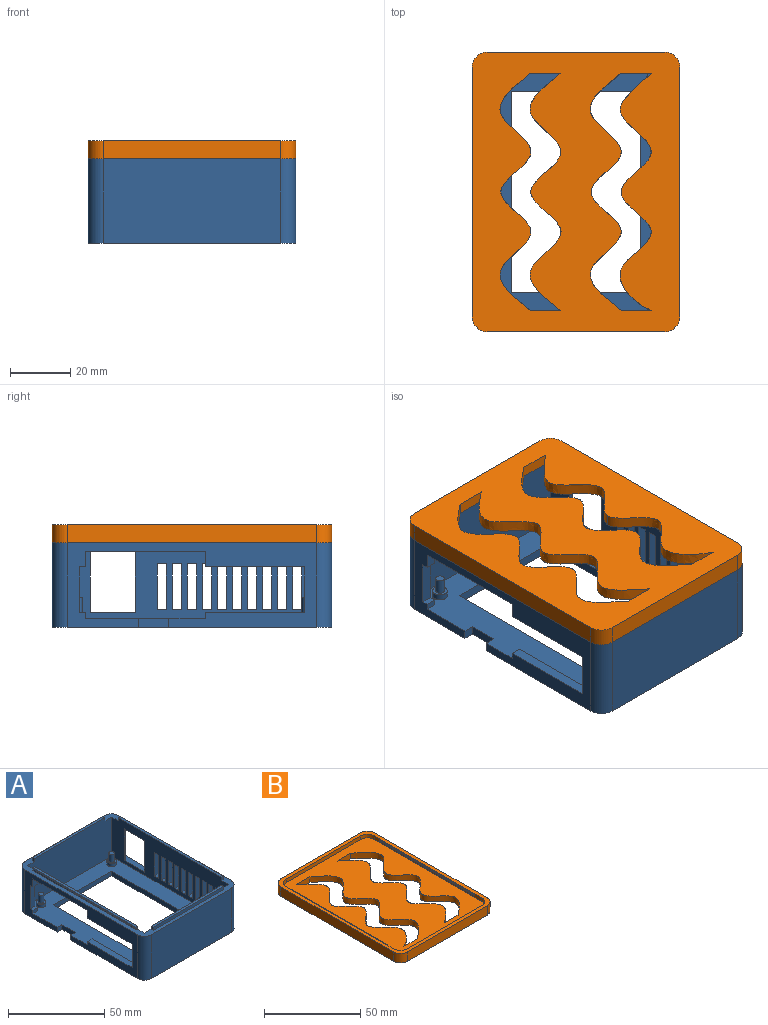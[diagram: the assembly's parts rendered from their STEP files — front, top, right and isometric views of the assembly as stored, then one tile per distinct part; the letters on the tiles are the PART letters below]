
ASSEMBLY  parts=2 mates=1
PART A: 119 faces, bbox 69x93x30 mm
  f0: plane 93x69mm, normal (0,0,1), area 755.5mm2, adj f3,f56,f57,f58,f86,f87,f88,f89
  f1: plane 20x1mm, normal (0,1,0), area 20mm2, adj f49,f50,f88,f96
  f2: plane 20x1mm, normal (0,-1,0), area 20mm2, adj f49,f50,f88,f94
  f3: plane 83x28mm, normal (1,0,0), area 1329mm2, adj f0,f6,f7,f8,f9,f10,f11,f12
  f4: plane 86x65.5mm, normal (0,0,1), area 2480.6mm2, adj f51,f52,f53,f54,f56,f59,f63,f67
  f5: plane 15x3.5mm, normal (0,1,0), area 52.5mm2, adj f46,f48,f88,f116
  f6: plane 3.5x3mm, normal (0,0,-1), area 10.5mm2, adj f3,f7,f8,f88
  f7: plane 15x3.5mm, normal (0,-1,0), area 52.5mm2, adj f3,f6,f9,f88
  f8: plane 15x3.5mm, normal (0,1,0), area 52.5mm2, adj f3,f6,f9,f88
  f9: plane 3.5x3mm, normal (0,0,1), area 10.5mm2, adj f3,f7,f8,f88
  f10: plane 3.5x3mm, normal (0,0,-1), area 10.5mm2, adj f3,f11,f12,f88
  f11: plane 15x3.5mm, normal (0,-1,0), area 52.5mm2, adj f3,f10,f13,f88
  f12: plane 15x3.5mm, normal (0,1,0), area 52.5mm2, adj f3,f10,f13,f88
  f13: plane 3.5x3mm, normal (0,0,1), area 10.5mm2, adj f3,f11,f12,f88
  f14: plane 3.5x3mm, normal (0,0,-1), area 10.5mm2, adj f3,f15,f16,f88
  f15: plane 15x3.5mm, normal (0,-1,0), area 52.5mm2, adj f3,f14,f17,f88
  f16: plane 15x3.5mm, normal (0,1,0), area 52.5mm2, adj f3,f14,f17,f88
  f17: plane 3.5x3mm, normal (0,0,1), area 10.5mm2, adj f3,f15,f16,f88
  f18: plane 3.5x3mm, normal (0,0,-1), area 10.5mm2, adj f3,f19,f20,f88
  f19: plane 15x3.5mm, normal (0,-1,0), area 52.5mm2, adj f3,f18,f21,f88
  f20: plane 15x3.5mm, normal (0,1,0), area 52.5mm2, adj f3,f18,f21,f88
  f21: plane 3.5x3mm, normal (0,0,1), area 10.5mm2, adj f3,f19,f20,f88
  f22: plane 3.5x3mm, normal (0,0,-1), area 10.5mm2, adj f3,f23,f24,f88
  f23: plane 15x3.5mm, normal (0,-1,0), area 52.5mm2, adj f3,f22,f25,f88
  f24: plane 15x3.5mm, normal (0,1,0), area 52.5mm2, adj f3,f22,f25,f88
  f25: plane 3.5x3mm, normal (0,0,1), area 10.5mm2, adj f3,f23,f24,f88
  f26: plane 3.5x3mm, normal (0,0,-1), area 10.5mm2, adj f3,f27,f28,f88
  f27: plane 15x3.5mm, normal (0,-1,0), area 52.5mm2, adj f3,f26,f29,f88
  f28: plane 15x3.5mm, normal (0,1,0), area 52.5mm2, adj f3,f26,f29,f88
  f29: plane 3.5x3mm, normal (0,0,1), area 10.5mm2, adj f3,f27,f28,f88
  f30: plane 3.5x3mm, normal (0,0,-1), area 10.5mm2, adj f3,f31,f32,f88
  f31: plane 15x3.5mm, normal (0,-1,0), area 52.5mm2, adj f3,f30,f33,f88
  f32: plane 15x3.5mm, normal (0,1,0), area 52.5mm2, adj f3,f30,f33,f88
  f33: plane 3.5x3mm, normal (0,0,1), area 10.5mm2, adj f3,f31,f32,f88
  f34: plane 3.5x3mm, normal (0,0,-1), area 10.5mm2, adj f3,f35,f36,f88
  f35: plane 15x3.5mm, normal (0,-1,0), area 52.5mm2, adj f3,f34,f37,f88
  f36: plane 15x3.5mm, normal (0,1,0), area 52.5mm2, adj f3,f34,f37,f88
  f37: plane 3.5x3mm, normal (0,0,1), area 10.5mm2, adj f3,f35,f36,f88
  f38: plane 3.5x3mm, normal (0,0,-1), area 10.5mm2, adj f3,f39,f40,f88
  f39: plane 15x3.5mm, normal (0,-1,0), area 52.5mm2, adj f3,f38,f41,f88
  f40: plane 15x3.5mm, normal (0,1,0), area 52.5mm2, adj f3,f38,f41,f88
  f41: plane 3.5x3mm, normal (0,0,1), area 10.5mm2, adj f3,f39,f40,f88
  f42: plane 3.5x3mm, normal (0,0,-1), area 10.5mm2, adj f3,f43,f44,f88
  f43: plane 15x3.5mm, normal (0,-1,0), area 52.5mm2, adj f3,f42,f45,f88
  f44: plane 15x3.5mm, normal (0,1,0), area 52.5mm2, adj f3,f42,f45,f88
  f45: plane 3.5x3mm, normal (0,0,1), area 10.5mm2, adj f3,f43,f44,f88
  f46: plane 3.5x3mm, normal (0,0,1), area 10.5mm2, adj f3,f5,f47,f88
  f47: plane 15x3.5mm, normal (0,-1,0), area 52.5mm2, adj f3,f46,f48,f88
  f48: plane 3.5x3mm, normal (0,0,-1), area 10.5mm2, adj f3,f5,f47,f88
  f49: plane 25x3.5mm, normal (0,0,-1), area 77.5mm2, adj f1,f2,f3,f88,f93,f94,f95,f96
  f50: plane 25x3.5mm, normal (0,0,1), area 77.5mm2, adj f1,f2,f3,f88,f93,f94,f95,f96
  f51: plane 43x3mm, normal (0,1,0), area 129mm2, adj f4,f52,f54,f55
  f52: plane 67x3mm, normal (1,0,0), area 201mm2, adj f4,f51,f53,f55
  f53: plane 43x3mm, normal (0,-1,0), area 129mm2, adj f4,f52,f54,f55
  f54: plane 67x3mm, normal (-1,0,0), area 201mm2, adj f4,f51,f53,f55
  f55: plane 93x69mm, normal (0,0,-1), area 3479.5mm2, adj f3,f51,f52,f53,f54,f56,f57,f58
  f56: plane 83x28mm, normal (-1,0,0), area 889mm2, adj f0,f4,f55,f75,f76,f77,f78,f79
  f57: plane 59x28mm, normal (0,-1,0), area 1652mm2, adj f0,f55,f115,f116
  f58: plane 59x28mm, normal (0,1,0), area 1652mm2, adj f0,f55,f117,f118
  f59: cylinder r=2.45mm len=4.9mm, axis (0,0,-1), area 30.8mm2, adj f4,f60
  f60: plane 4.9x4.9mm, normal (0,0,1), area 12.3mm2, adj f59,f62
  f61: plane 2.9x2.9mm, normal (0,0,1), area 6.6mm2, adj f62
  f62: cylinder r=1.45mm len=5mm, axis (0,0,-1), area 45.6mm2, adj f60,f61
  f63: cylinder r=2.45mm len=4.9mm, axis (0,0,-1), area 30.8mm2, adj f4,f64
  f64: plane 4.9x4.9mm, normal (0,0,1), area 12.3mm2, adj f63,f66
  f65: plane 2.9x2.9mm, normal (0,0,1), area 6.6mm2, adj f66
  f66: cylinder r=1.45mm len=5mm, axis (0,0,-1), area 45.6mm2, adj f64,f65
  f67: cylinder r=2.45mm len=4.9mm, axis (0,0,-1), area 30.8mm2, adj f4,f68
  f68: plane 4.9x4.9mm, normal (0,0,1), area 12.3mm2, adj f67,f70
  f69: plane 2.9x2.9mm, normal (0,0,1), area 6.6mm2, adj f70
  f70: cylinder r=1.45mm len=5mm, axis (0,0,-1), area 45.6mm2, adj f68,f69
  f71: cylinder r=2.45mm len=4.9mm, axis (0,0,-1), area 30.8mm2, adj f4,f72
  f72: plane 4.9x4.9mm, normal (0,0,1), area 12.3mm2, adj f71,f74
  f73: plane 2.9x2.9mm, normal (0,0,1), area 6.6mm2, adj f74
  f74: cylinder r=1.45mm len=5mm, axis (0,0,-1), area 45.6mm2, adj f72,f73
  f75: plane 5x3.5mm, normal (0,1,0), area 17.5mm2, adj f56,f76,f84,f86
  f76: plane 40x3.5mm, normal (0,0,-1), area 140mm2, adj f56,f75,f77,f86
  f77: plane 5x3.5mm, normal (0,-1,0), area 17.5mm2, adj f56,f76,f78,f86
  f78: plane 3.5x2mm, normal (0,0,-1), area 7mm2, adj f56,f77,f79,f86
  f79: plane 15x3.5mm, normal (0,-1,0), area 52.5mm2, adj f56,f78,f80,f86
  f80: plane 3.5x2mm, normal (0,0,1), area 7mm2, adj f56,f79,f81,f86
  f81: plane 3.5x2mm, normal (0,-1,0), area 7mm2, adj f4,f56,f80,f86
  f82: plane 3.5x2mm, normal (0,1,0), area 7mm2, adj f4,f56,f83,f86
  f83: plane 33x3.5mm, normal (0,0,1), area 115.5mm2, adj f56,f82,f85,f86
  f84: plane 33x3.5mm, normal (0,0,-1), area 115.5mm2, adj f56,f75,f85,f86
  f85: plane 15x3.5mm, normal (0,1,0), area 52.5mm2, adj f56,f83,f84,f86
  f86: plane 86x27mm, normal (1,0,0), area 897mm2, adj f0,f4,f75,f76,f77,f78,f79,f80
  f87: plane 62x27mm, normal (0,1,0), area 1654mm2, adj f0,f4,f86,f88,f107,f109,f110
  f88: plane 86x27mm, normal (-1,0,0), area 1507mm2, adj f0,f1,f2,f4,f5,f6,f7,f8
  f89: plane 62x27mm, normal (0,-1,0), area 1654mm2, adj f0,f4,f86,f88,f112,f113,f114
  f90: plane 3.5x3mm, normal (0,1,0), area 10.5mm2, adj f4,f55,f56,f92
  f91: plane 3.5x3mm, normal (0,-1,0), area 10.5mm2, adj f4,f55,f56,f92
  f92: plane 10x3mm, normal (-1,0,0), area 30mm2, adj f4,f55,f90,f91
  f93: plane 20x2.5mm, normal (0,-1,0), area 50mm2, adj f3,f49,f50,f94
  f94: plane 20x5mm, normal (1,0,0), area 100mm2, adj f2,f49,f50,f93
  f95: plane 20x2.5mm, normal (0,1,0), area 50mm2, adj f3,f49,f50,f96
  f96: plane 20x5mm, normal (1,0,0), area 100mm2, adj f1,f49,f50,f95
  f97: plane 76x1.5mm, normal (0,0,1), area 114mm2, adj f86,f98,f100,f101
  f98: cylinder r=1.22mm len=76mm, axis (0,1,0), area 88.3mm2, adj f97,f99,f100,f101
  f99: plane 76x1mm, normal (-1,0,0), area 76mm2, adj f0,f98,f100,f101
  f100: plane 2x1.5mm, normal (0,-1,0), area 2.4mm2, adj f0,f86,f97,f98,f99
  f101: plane 2x1.5mm, normal (0,1,0), area 2.4mm2, adj f0,f86,f97,f98,f99
  f102: plane 76x1mm, normal (1,0,0), area 76mm2, adj f0,f103,f105,f106
  f103: cylinder r=1.22mm len=76mm, axis (0,1,0), area 88.3mm2, adj f102,f104,f105,f106
  f104: plane 76x1.5mm, normal (0,0,1), area 114mm2, adj f88,f103,f105,f106
  f105: plane 2x1.5mm, normal (0,-1,0), area 2.4mm2, adj f0,f88,f102,f103,f104
  f106: plane 2x1.5mm, normal (0,1,0), area 2.4mm2, adj f0,f88,f102,f103,f104
  f107: plane 52x1.5mm, normal (0,0,1), area 78mm2, adj f87,f108,f109,f110
  f108: plane 52x2mm, normal (0,-1,0), area 104mm2, adj f0,f107,f109,f110
  f109: plane 2x1.5mm, normal (1,0,0), area 3mm2, adj f0,f87,f107,f108
  f110: plane 2x1.5mm, normal (-1,0,0), area 3mm2, adj f0,f87,f107,f108
  f111: plane 52x2mm, normal (0,1,0), area 104mm2, adj f0,f112,f113,f114
  f112: plane 52x1.5mm, normal (0,0,1), area 78mm2, adj f89,f111,f113,f114
  f113: plane 2x1.5mm, normal (1,0,0), area 3mm2, adj f0,f89,f111,f112
  f114: plane 2x1.5mm, normal (-1,0,0), area 3mm2, adj f0,f89,f111,f112
  f115: cylinder r=5mm len=28mm, axis (0,0,-1), area 219.9mm2, adj f0,f55,f56,f57
  f116: cylinder r=5mm len=28mm, axis (0,0,-1), area 219.9mm2, adj f0,f3,f5,f55,f57
  f117: cylinder r=5mm len=28mm, axis (0,0,-1), area 219.9mm2, adj f0,f3,f55,f58
  f118: cylinder r=5mm len=28mm, axis (0,0,-1), area 219.9mm2, adj f0,f55,f56,f58
PART B: 39 faces, bbox 69x93x6 mm
  f0: plane 93x69mm, normal (0,0,-1), area 4818.6mm2, adj f2,f3,f4,f5,f21,f22,f23,f24
  f1: plane 89x65mm, normal (0,0,1), area 4186.6mm2, adj f7,f8,f9,f10,f21,f22,f23,f24
  f2: plane 83x6mm, normal (-1,0,0), area 498mm2, adj f0,f6,f31,f34
  f3: plane 59x6mm, normal (0,-1,0), area 354mm2, adj f0,f6,f31,f32
  f4: plane 83x6mm, normal (1,0,0), area 498mm2, adj f0,f6,f32,f33
  f5: plane 59x6mm, normal (0,1,0), area 354mm2, adj f0,f6,f33,f34
  f6: plane 93x69mm, normal (0,0,1), area 632mm2, adj f2,f3,f4,f5,f7,f8,f9,f10
  f7: plane 79x2.3mm, normal (1,0,0), area 92.4mm2, adj f1,f6,f12,f14,f15,f35,f38
  f8: plane 55x2.3mm, normal (0,1,0), area 126.5mm2, adj f1,f6,f35,f36
  f9: plane 79x2.3mm, normal (-1,0,0), area 92.4mm2, adj f1,f6,f16,f19,f20,f36,f37
  f10: plane 55x2.3mm, normal (0,-1,0), area 126.5mm2, adj f1,f6,f37,f38
  f11: plane 70x0.43mm, normal (1,0,0), area 29.8mm2, adj f12,f13,f14,f15
  f12: cylinder r=0.42mm len=70mm, axis (0,-1,0), area 46.7mm2, adj f7,f11,f14,f15
  f13: cylinder r=0.42mm len=70mm, axis (0,-1,0), area 46.7mm2, adj f6,f11,f14,f15
  f14: plane 1.28x0.43mm, normal (0,1,0), area 0.5mm2, adj f7,f11,f12,f13
  f15: plane 1.28x0.43mm, normal (0,-1,0), area 0.5mm2, adj f7,f11,f12,f13
  f16: cylinder r=0.42mm len=70mm, axis (0,-1,0), area 46.7mm2, adj f9,f17,f19,f20
  f17: plane 70x0.43mm, normal (-1,0,0), area 29.8mm2, adj f16,f18,f19,f20
  f18: cylinder r=0.42mm len=70mm, axis (0,-1,0), area 46.7mm2, adj f6,f17,f19,f20
  f19: plane 1.28x0.43mm, normal (0,1,0), area 0.5mm2, adj f9,f16,f17,f18
  f20: plane 1.28x0.43mm, normal (0,-1,0), area 0.5mm2, adj f9,f16,f17,f18
  f21: extruded ~79x10.23mm, area 382.7mm2, adj f0,f1,f22,f24
  f22: plane 10x3.7mm, normal (0,1,0), area 37mm2, adj f0,f1,f21,f23
  f23: extruded ~79x10.23mm, area 382.7mm2, adj f0,f1,f22,f24
  f24: plane 10x3.7mm, normal (0,-1,0), area 37mm2, adj f0,f1,f21,f23
  f25: plane 10x3.7mm, normal (0,1,0), area 37mm2, adj f0,f1,f26,f30
  f26: extruded ~39.48x10.31mm, area 191.4mm2, adj f0,f1,f25,f27
  f27: plane 3.7x0.02mm, normal (1,0,0), area 0.1mm2, adj f0,f1,f26,f28
  f28: extruded ~39.5x10.22mm, area 189.3mm2, adj f0,f1,f27,f29
  f29: plane 10x3.7mm, normal (0,-1,0), area 37mm2, adj f0,f1,f28,f30
  f30: extruded ~79x10.23mm, area 382.7mm2, adj f0,f1,f25,f29
  f31: cylinder r=5mm len=6mm, axis (0,0,-1), area 47.1mm2, adj f0,f2,f3,f6
  f32: cylinder r=5mm len=6mm, axis (0,0,1), area 47.1mm2, adj f0,f3,f4,f6
  f33: cylinder r=5mm len=6mm, axis (0,0,-1), area 47.1mm2, adj f0,f4,f5,f6
  f34: cylinder r=5mm len=6mm, axis (0,0,1), area 47.1mm2, adj f0,f2,f5,f6
  f35: cylinder r=5mm len=5mm, axis (0,0,-1), area 18.1mm2, adj f1,f6,f7,f8
  f36: cylinder r=5mm len=5mm, axis (0,0,1), area 18.1mm2, adj f1,f6,f8,f9
  f37: cylinder r=5mm len=5mm, axis (0,0,-1), area 18.1mm2, adj f1,f6,f9,f10
  f38: cylinder r=5mm len=5mm, axis (0,0,1), area 18.1mm2, adj f1,f6,f7,f10
PLACE A t=(-25.66,-67.4,67.17)mm
PLACE B rot(axis=(0,1,0),180deg) t=(38.34,20.6,101.17)mm
MATE slider A.f0 <-> B.f6  axis (0,0,1) through (3.84,-25.9,95.17)mm
